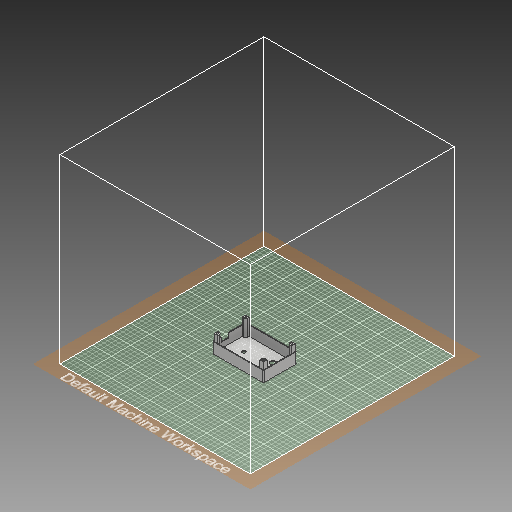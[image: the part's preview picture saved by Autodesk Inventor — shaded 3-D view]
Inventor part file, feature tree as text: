
AUTODESK INVENTOR PART (.ipt)
format: ipt  version: 2019 (Build 230136000, 136)  size: 418,816 bytes
history: native  units: mm
features: other x8, extrude x5, hole x1, fillet x1, loft x1, sketch x1
ambient origin geometry x8: Origin, YZ Plane, XZ Plane, XY Plane, X Axis, Y Axis, Z Axis, Center Point
bodies: Solid1 (feature_tree)
feature tree (17):
  extrude  "Extrusion1"  Depth=70.0mm
  other  "stena_RJ45"
  extrude  "Extrusion2"  Depth=1.2mm TaperAngle=0.0deg
  extrude  "Extrusion3"  Depth=1.6mm
  extrude  "Extrusion4"  Depth=16.8mm
  extrude  "Extrusion5"  Depth=15.7mm
  hole  "Hole1"  [1 undecoded]
  fillet  "Fillet1"  Radius=11.5mm
  other  "znacka_napajeni1"
  other  "rovina_napajeni_znacka2"
  loft  "Loft1"
  other  "zakladna"
  other  "diry_tlacirka_LED"
  other  "steny"
  sketch  "Sketch5"  dims[d0=109.0mm d1=70.0mm d2=1.2mm d3=0.0mm d4=1.6mm d5=16.8mm d6=15.7mm d7=0.0mm d9=11.5mm d10=7.7mm d11=31.0mm d12=2.0mm d13=0.0mm d18=23.4mm d19=0.0mm d20=13.6mm d21=0.0mm d22=8.0mm d27=36.8mm d28=0.0mm d29=3.3mm d30=6.0mm d31=3.75mm d32=2.0mm d33=1.745329mm d34=12.0mm d35=0.0mm d36=0.4mm d37=0.0mm d42=1.6mm d43=2.0mm d44=0.8mm d45=1.0mm d46=18.0mm d47=-0.5mm d48=0.0mm d49=90.0deg d50=0.0mm d51=90.0deg d53=25.0mm]
  other  "diry_zavitova_vlozka"
  other  "napajeni_znacka2"
note: 1 required parameter value undecoded (feature->parameter linkage not recoverable at this tier; creation-order binding heuristic only, values carry confidence <= 0.55)
